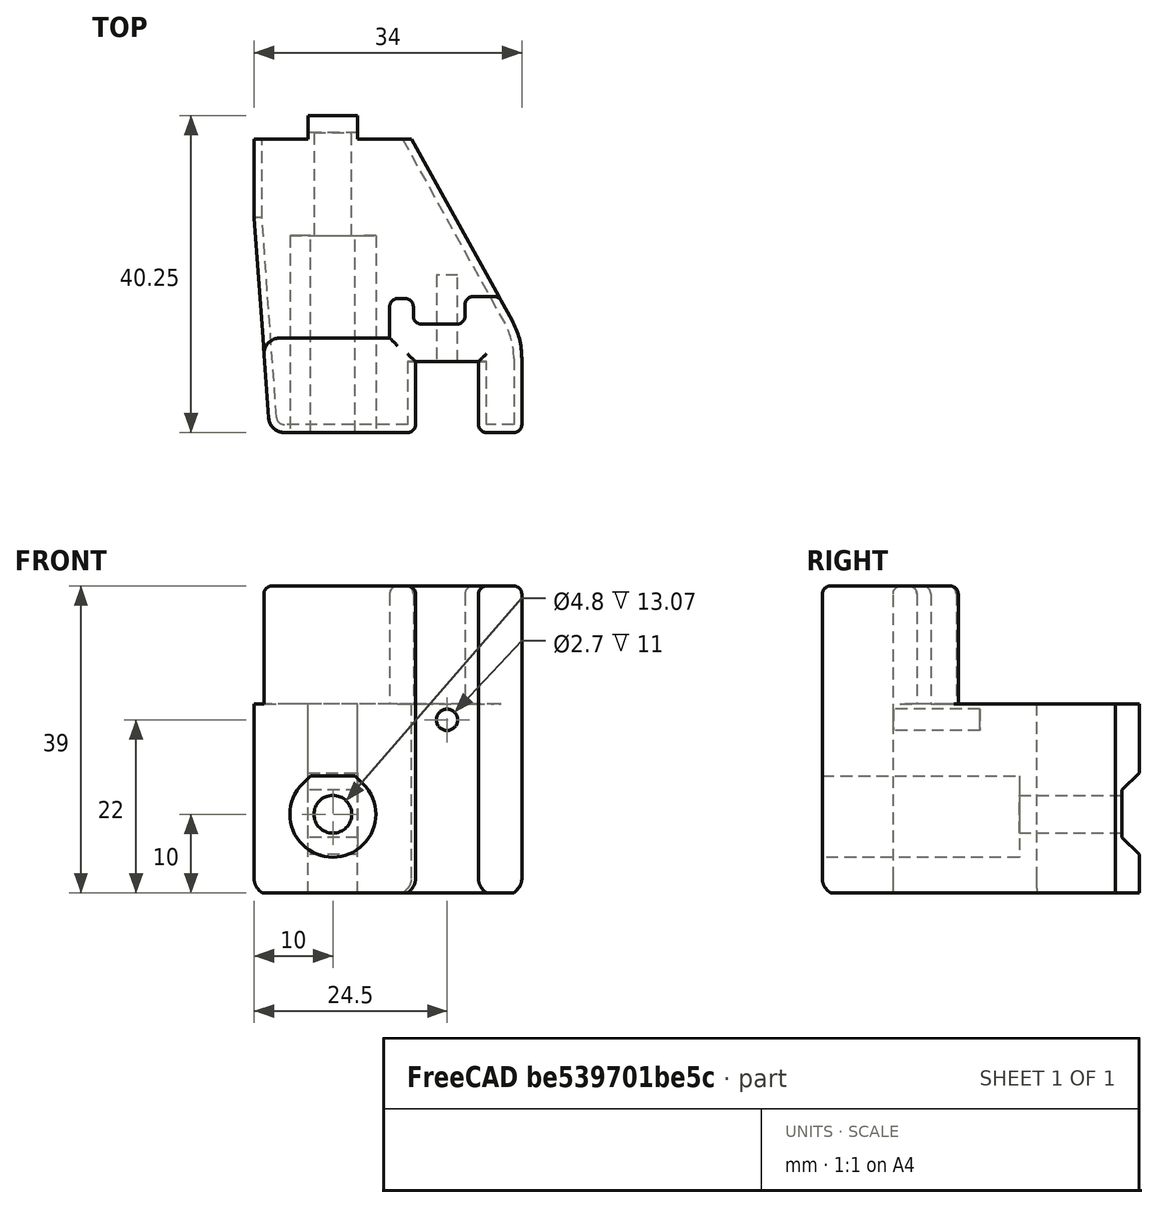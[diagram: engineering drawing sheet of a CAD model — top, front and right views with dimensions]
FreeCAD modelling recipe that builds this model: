
FCSTD DOCUMENT  (FreeCAD 0.19R)
Label: Zmount3
License: All rights reserved
LicenseURL: http://en.wikipedia.org/wiki/All_rights_reserved
objects: Sketcher::SketchObject×8, PartDesign::Pocket×6, PartDesign::Fillet×6, PartDesign::Chamfer×2, PartDesign::Pad×1, PartDesign::Body×1, Mesh::Feature×1
note: 39 computed .brp shape members not serialized (recipe doc carries the construction recipe); baked Part::Feature solids carry a one-line shape summary decoded from their .brp

FEATURE [Sketcher::SketchObject] Sketch
  FullyConstrained = false
  MapMode = 5
  Support = -> [XY_Plane]
  sketch-geometry (10):
    g0: LineSegment StartX=-10 StartY=2e-16 StartZ=0 EndX=-3.15 EndY=2e-16 EndZ=0
    g1: LineSegment StartX=-3.15 StartY=2e-16 StartZ=0 EndX=-3.15 EndY=3 EndZ=0
    g2: LineSegment StartX=-3.15 StartY=3 StartZ=0 EndX=3.15 EndY=3 EndZ=0
    g3: LineSegment StartX=3.15 StartY=3 StartZ=0 EndX=3.15 EndY=0 EndZ=0
    g4: LineSegment StartX=3.15 StartY=0 StartZ=0 EndX=10 EndY=0 EndZ=0
    g5: LineSegment StartX=24 StartY=-37.25 StartZ=0 EndX=-8.02191 EndY=-37.25 EndZ=0
    g6: LineSegment StartX=24 StartY=-25.25 StartZ=0 EndX=24 EndY=-37.25 EndZ=0
    g7: LineSegment StartX=10 StartY=0 StartZ=0 EndX=24 EndY=-25.25 EndZ=0
    g8: LineSegment StartX=-8.02191 StartY=-37.25 StartZ=0 EndX=-10 EndY=-10 EndZ=0
    g9: LineSegment StartX=-10 StartY=2e-16 StartZ=0 EndX=-10 EndY=-10 EndZ=0
  constraints (28):
    c: Horizontal(g0)
    c: Coincident(g0,g1)
    c: Coincident(g1,g2)
    c: Coincident(g2,g3)
    c: Vertical(g3)
    c: Coincident(g3,g4)
    c: Horizontal(g4)
    c: Horizontal(g5)
    c: Distance(g2) = 6.3
    c: Vertical(g1)
    c: Distance(g3) = 3
    c: Equal(g1,g3)
    c: PointOnObject(g3,g-1)
    c: DistanceX(g0) = -10
    c: DistanceY(g5) = -37.25
    c: DistanceX(g4) = 10
    c: Vertical(g6)
    c: Coincident(g5,g6)
    c: DistanceX(g6) = 24
    c: Coincident(g7,g4)
    c: Coincident(g7,g6)
    c: Distance(g6) = 12
    c: Symmetric(g2,g1,g-2)
    c: Coincident(g8,g5)
    c: Coincident(g9,g0)
    c: Coincident(g9,g8)
    c: Vertical(g9)
    c: Distance(g9) = 10
FEATURE [PartDesign::Pad] Pad
  Direction = (1,1,1)
  Length = 39
  Length2 = 100
  Profile = -> Sketch
  Type = 0
FEATURE [Sketcher::SketchObject] Sketch001
  ExternalGeometry = -> [Pad]
  FullyConstrained = false
  MapMode = 5
  Placement = pos=(0,0,39) rot=(0,0,1;0rad)
  Support = -> [Pad]
  sketch-geometry (10):
    g0: LineSegment StartX=-13.62 StartY=24.0751 StartZ=0 EndX=22.1616 EndY=24.0751 EndZ=0
    g1: LineSegment StartX=22.1616 StartY=24.0751 StartZ=0 EndX=22.1616 EndY=-19.9944 EndZ=0
    g2: LineSegment StartX=-13.62 StartY=-25.25 StartZ=0 EndX=-13.62 EndY=24.0751 EndZ=0
    g3: LineSegment StartX=7.22052 StartY=-20.25 StartZ=0 EndX=7.22052 EndY=-25.25 EndZ=0
    g4: LineSegment StartX=7.22052 StartY=-25.25 StartZ=0 EndX=-13.62 EndY=-25.25 EndZ=0
    g5: LineSegment StartX=7.22052 StartY=-20.25 StartZ=0 EndX=10.2205 EndY=-20.25 EndZ=0
    g6: LineSegment StartX=10.2205 StartY=-20.25 StartZ=0 EndX=10.2205 EndY=-23.4787 EndZ=0
    g7: LineSegment StartX=10.2205 StartY=-23.4787 StartZ=0 EndX=16.7949 EndY=-23.4787 EndZ=0
    g8: LineSegment StartX=16.7949 StartY=-23.4787 StartZ=0 EndX=16.7949 EndY=-19.9944 EndZ=0
    g9: LineSegment StartX=16.7949 StartY=-19.9944 StartZ=0 EndX=22.1616 EndY=-19.9944 EndZ=0
  constraints (23):
    c: Coincident(g0,g1)
    c: Coincident(g2,g0)
    c: Horizontal(g0)
    c: Vertical(g1)
    c: Vertical(g2)
    c: Coincident(g3,g4)
    c: Coincident(g4,g2)
    c: Horizontal(g4)
    c: Distance(g3) = 5
    c: Vertical(g3)
    c: Distance(g-3,g4) = 12
    c: Coincident(g3,g5)
    c: Coincident(g5,g6)
    c: Vertical(g6)
    c: Coincident(g6,g7)
    c: Horizontal(g7)
    c: Coincident(g7,g8)
    c: Vertical(g8)
    c: Coincident(g8,g9)
    c: Coincident(g1,g9)
    c: Horizontal(g9)
    c: Distance(g5) = 3
    c: Horizontal(g5)
FEATURE [PartDesign::Pocket] Pocket  label="wave"
  BaseFeature = -> Pad
  Length = 15
  Length2 = 100
  Profile = -> Sketch001
  Type = 0
FEATURE [Sketcher::SketchObject] Sketch005
  ExternalGeometry = -> [Pocket]
  FullyConstrained = true
  MapMode = 5
  Placement = pos=(0,-37.25,0) rot=(1,0,0;1.5708rad)
  Support = -> [Pocket]
  sketch-geometry (1):
    g0: Circle CenterX=14.5 CenterY=22 CenterZ=0 NormalX=0 NormalY=0 NormalZ=1 AngleXU=0 Radius=1.35
  constraints (3):
    c: Diameter(g0) = 2.7
    c: DistanceX(g0) = 14.5
    c: Distance(g0,g-4) = 17
FEATURE [PartDesign::Pocket] Pocket001
  BaseFeature = -> Pocket
  Length = 20
  Length2 = 100
  Profile = -> Sketch005
  Type = 0
FEATURE [Sketcher::SketchObject] Sketch006
  FullyConstrained = true
  MapMode = 5
  Placement = pos=(0,3,0) rot=(0,0.707107,0.707107;3.14159rad)
  sketch-geometry (1):
    g0: Circle CenterX=0 CenterY=10 CenterZ=0 NormalX=0 NormalY=0 NormalZ=1 AngleXU=0 Radius=2.4
  constraints (4):
    c: PointOnObject(g0,g-2)
    c: DistanceY(g0) = 10
    c: Block(g0)
    c: Diameter(g0) = 4.8
FEATURE [Sketcher::SketchObject] Sketch008
  ExternalGeometry = -> [Pocket001]
  FullyConstrained = false
  MapMode = 5
  Placement = pos=(0,-37.25,0) rot=(1,0,0;1.5708rad)
  Support = -> [Pocket001]
  sketch-geometry (4):
    g0: LineSegment StartX=10.5 StartY=39.1817 StartZ=0 EndX=18.5 EndY=39.1817 EndZ=0
    g1: LineSegment StartX=18.5 StartY=39.1817 StartZ=0 EndX=18.5 EndY=-4.25952 EndZ=0
    g2: LineSegment StartX=18.5 StartY=-4.25952 StartZ=0 EndX=10.5 EndY=-4.25952 EndZ=0
    g3: LineSegment StartX=10.5 StartY=-4.25952 StartZ=0 EndX=10.5 EndY=39.1817 EndZ=0
  constraints (9):
    c: Coincident(g0,g1)
    c: Coincident(g1,g2)
    c: Coincident(g2,g3)
    c: Coincident(g3,g0)
    c: Horizontal(g0)
    c: Horizontal(g2)
    c: Vertical(g1)
    c: Vertical(g3)
    c: Distance(g0) = 8
FEATURE [PartDesign::Pocket] Pocket002  label="notch"
  BaseFeature = -> Pocket001
  Length = 9
  Length2 = 100
  Profile = -> Sketch008
  Type = 0
FEATURE [PartDesign::Pocket] Pocket003
  BaseFeature = -> Pocket002
  Length = 5
  Length2 = 100
  Profile = -> Sketch006
  Type = 1
FEATURE [Sketcher::SketchObject] Sketch009
  ExternalGeometry = -> [Pocket003]
  FullyConstrained = false
  MapMode = 5
  Placement = pos=(0,-37.25,0) rot=(1,0,0;1.5708rad)
  Support = -> [Pocket003]
  sketch-geometry (3):
    g0: LineSegment StartX=0 StartY=17.7224 StartZ=0 EndX=-3.86121 EndY=13.8612 EndZ=0
    g1: LineSegment StartX=0 StartY=17.7224 StartZ=0 EndX=3.86121 EndY=13.8612 EndZ=0
    g2: ArcOfCircle CenterX=-1e-16 CenterY=10 CenterZ=0 NormalX=0 NormalY=0 NormalZ=1 AngleXU=0 Radius=5.46057 StartAngle=2.35619 EndAngle=7.06858
  constraints (5):
    c: PointOnObject(g0,g-2)
    c: Coincident(g0,g1)
    c: Tangent(g2,g0) = -1.5708
    c: Tangent(g2,g1) = 1.5708
    c: Perpendicular(g0,g1)
FEATURE [PartDesign::Pocket] Pocket004
  BaseFeature = -> Pocket003
  Length = 25
  Length2 = 100
  Profile = -> Sketch009
  Type = 0
FEATURE [Sketcher::SketchObject] Sketch010
  FullyConstrained = true
  MapMode = 5
  Placement = pos=(0,3,0) rot=(0,0.707107,0.707107;3.14159rad)
FEATURE [Sketcher::SketchObject] Sketch011
  FullyConstrained = false
  MapMode = 5
  Placement = pos=(3.15,0,0) rot=(0.57735,0.57735,0.57735;2.0944rad)
  Support = -> [Pocket004]
  sketch-geometry (4):
    g0: LineSegment StartX=7.56983 StartY=19.8125 StartZ=0 EndX=0.82022 EndY=13.0629 EndZ=0
    g1: LineSegment StartX=0.82022 StartY=13.0629 StartZ=0 EndX=0.82022 EndY=7.06294 EndZ=0
    g2: LineSegment StartX=0.82022 StartY=7.06294 StartZ=0 EndX=10.0672 EndY=-2.18402 EndZ=0
    g3: LineSegment StartX=10.0672 StartY=-2.18402 StartZ=0 EndX=7.56983 EndY=19.8125 EndZ=0
  constraints (8):
    c: Coincident(g0,g1)
    c: Vertical(g1)
    c: Coincident(g1,g2)
    c: Coincident(g2,g3)
    c: Coincident(g3,g0)
    c: Distance(g1) = 6
    c: Angle(g0) = -2.35619
    c: Angle(g2) = -0.785398
FEATURE [PartDesign::Pocket] Pocket005
  BaseFeature = -> Pocket004
  Length = 5
  Length2 = 100
  Profile = -> Sketch011
  Type = 1
FEATURE [PartDesign::Fillet] Fillet
  Base = -> Pocket005 [Edge54,Edge58,Edge78,Edge72,Edge71,Edge74,Edge76,Edge41,Edge51]
  BaseFeature = -> Pocket005
  Radius = 1
  SupportTransform = false
FEATURE [PartDesign::Fillet] Fillet001
  Base = -> Fillet [Edge19,Edge28]
  BaseFeature = -> Fillet
  Radius = 2
  SupportTransform = false
FEATURE [PartDesign::Fillet] Fillet002
  Base = -> Fillet001 [Edge71]
  BaseFeature = -> Fillet001
  Radius = 11
  SupportTransform = false
FEATURE [PartDesign::Fillet] Fillet003
  Base = -> Fillet001 [Edge67]
  BaseFeature = -> Fillet001
  Radius = 10
  SupportTransform = false
FEATURE [PartDesign::Chamfer] Chamfer
  Angle = 45
  Base = -> Fillet003 [Edge4,Edge18]
  BaseFeature = -> Fillet003
  ChamferType = 0
  FlipDirection = false
  Size = 1
  Size2 = 1
  SupportTransform = false
FEATURE [PartDesign::Fillet] Fillet004
  Base = -> Chamfer [Edge60,Edge23]
  BaseFeature = -> Chamfer
  Radius = 2
  SupportTransform = false
FEATURE [PartDesign::Fillet] Fillet005
  Base = -> Fillet004 [Face23]
  BaseFeature = -> Fillet004
  Radius = 1
  SupportTransform = false
FEATURE [PartDesign::Chamfer] Chamfer001
  Angle = 45
  Base = -> Fillet005 [Edge238]
  BaseFeature = -> Fillet005
  ChamferType = 0
  FlipDirection = false
  Size = 4
  Size2 = 1
  SupportTransform = false
FEATURE [PartDesign::Body] Body
  Group = -> [Sketch,Pad,Sketch001,Pocket,Sketch005,Pocket001,Sketch006,Sketch008,Pocket002,Pocket003,Sketch009,Pocket004,Sketch010,Sketch011,Pocket005,Fillet,Fillet001,Fillet002,Fillet003,Chamfer,Fillet004,Fillet005,Chamfer001]
  Origin = -> Origin
  Tip = -> Chamfer001
FEATURE [Mesh::Feature] Mesh  label="Chamfer001 (Meshed)"
